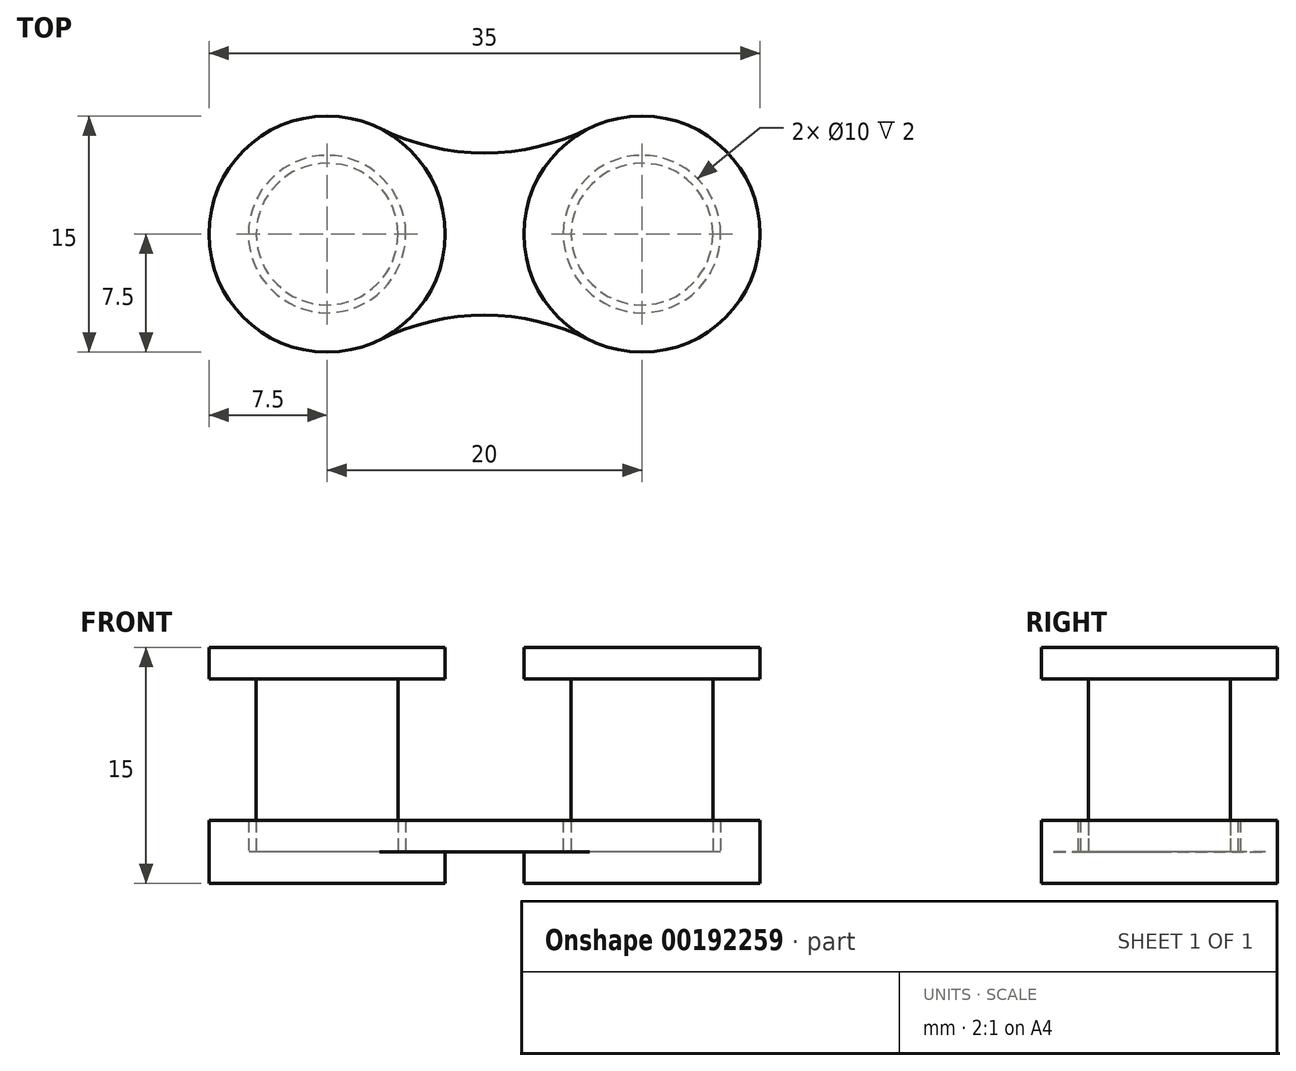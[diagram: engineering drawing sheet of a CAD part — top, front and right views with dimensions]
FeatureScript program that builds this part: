
annotation { "Feature Type Name" : "Feature", "Feature Type Description" : "" }
export const myFeature = defineFeature(function(context is Context, id is Id, definition is map)
    precondition{}
    {
        {
            var Q0;
            Q0=qCreatedBy(makeId("Top.planeOp"),FACE);
            var sketch = newSketch(context, id + "F0", { "sketchPlane" : qUnion([Q0])});
            skCircle(sketch, "E0", {"center": v(0, 0) * mm, "radius": 5 * mm});
            skCircle(sketch, "E1", {"center": v(20, 0) * mm, "radius": 5 * mm});
            skArc(sketch, "E2", {"start": v(3.33, 6.72) * mm, "mid": v(-7.5, 0) * mm, "end": v(3.33, -6.72) * mm});
            skArc(sketch, "E3", {"start": v(16.67, -6.72) * mm, "mid": v(27.5, 0) * mm, "end": v(16.67, 6.72) * mm});
            skArc(sketch, "E4", {"start": v(3.33, 6.72) * mm, "mid": v(10, 5.16) * mm, "end": v(16.67, 6.72) * mm});
            skArc(sketch, "E5", {"start": v(16.67, -6.72) * mm, "mid": v(10, -5.16) * mm, "end": v(3.33, -6.72) * mm});
            skSolve(sketch);
        }
        {
            var Q0;
            Q0=makeQuery(id+"F0.imprint","IMPRINT",FACE,{"disambiguationData":[TD([[makeQuery(id+"F0.imprint","IMPRINT",EDGE,{"derivedFrom":sQuery(id+"F0.wireOp",EDGE,"E0")}),-1.0]])]});
            extrude(context, id + "F1", {"entities" : qUnion([Q0]), "depth" : 2 * mm});
        }
        {
            var Q0;
            Q0=qCreatedBy(makeId("Top.planeOp"),FACE);
            var sketch = newSketch(context, id + "F2", { "sketchPlane" : qUnion([Q0])});
            skCircle(sketch, "E6", {"center": v(0, 0) * mm, "radius": 4.5 * mm});
            skCircle(sketch, "E7", {"center": v(20, 0) * mm, "radius": 4.5 * mm});
            skSolve(sketch);
        }
        {
            var Q0;
            Q0=makeQuery(id+"F2.imprint","IMPRINT",FACE,{"disambiguationData":[TD([[makeQuery(id+"F2.imprint","IMPRINT",EDGE,{"derivedFrom":sQuery(id+"F2.wireOp",EDGE,"E6")}),1.0]])]});
            var Q1;
            Q1=makeQuery(id+"F2.imprint","IMPRINT",FACE,{"disambiguationData":[TD([[makeQuery(id+"F2.imprint","IMPRINT",EDGE,{"derivedFrom":sQuery(id+"F2.wireOp",EDGE,"E7")}),1.0]])]});
            extrude(context, id + "F3", {"entities" : qUnion([Q0, Q1]), "depth" : 11 * mm});
        }
        {
            var Q0;
            Q0=makeQuery(id+"F3.opExtrude","CAP_FACE",FACE,{"disambiguationData":[OSD([sQuery(id+"F2.wireOp",EDGE,"E6")])],"isStart":false});
            var sketch = newSketch(context, id + "F4", { "sketchPlane" : qUnion([Q0])});
            skCircle(sketch, "E8", {"center": v(0, 0) * mm, "radius": 7.5 * mm});
            skCircle(sketch, "E9", {"center": v(20, 0) * mm, "radius": 7.5 * mm});
            skSolve(sketch);
        }
        {
            var Q0;
            Q0=qSketchRegion(id+"F4",true);
            extrude(context, id + "F5", {"entities" : qUnion([Q0]), "operationType" : NewBodyOperationType.ADD, "depth" : 2 * mm});
        }
        {
            var Q0;
            Q0=makeQuery(id+"F3.opExtrude","CAP_FACE",FACE,{"disambiguationData":[OSD([sQuery(id+"F2.wireOp",EDGE,"E6")])],"isStart":true});
            var sketch = newSketch(context, id + "F6", { "sketchPlane" : qUnion([Q0])});
            skCircle(sketch, "E10", {"center": v(0, 0) * mm, "radius": 7.5 * mm});
            skCircle(sketch, "E11", {"center": v(20, 0) * mm, "radius": 7.5 * mm});
            skSolve(sketch);
        }
        {
            var Q0;
            Q0=qSketchRegion(id+"F6",true);
            extrude(context, id + "F7", {"entities" : qUnion([Q0]), "operationType" : NewBodyOperationType.ADD, "depth" : 2 * mm});
        }
    });
